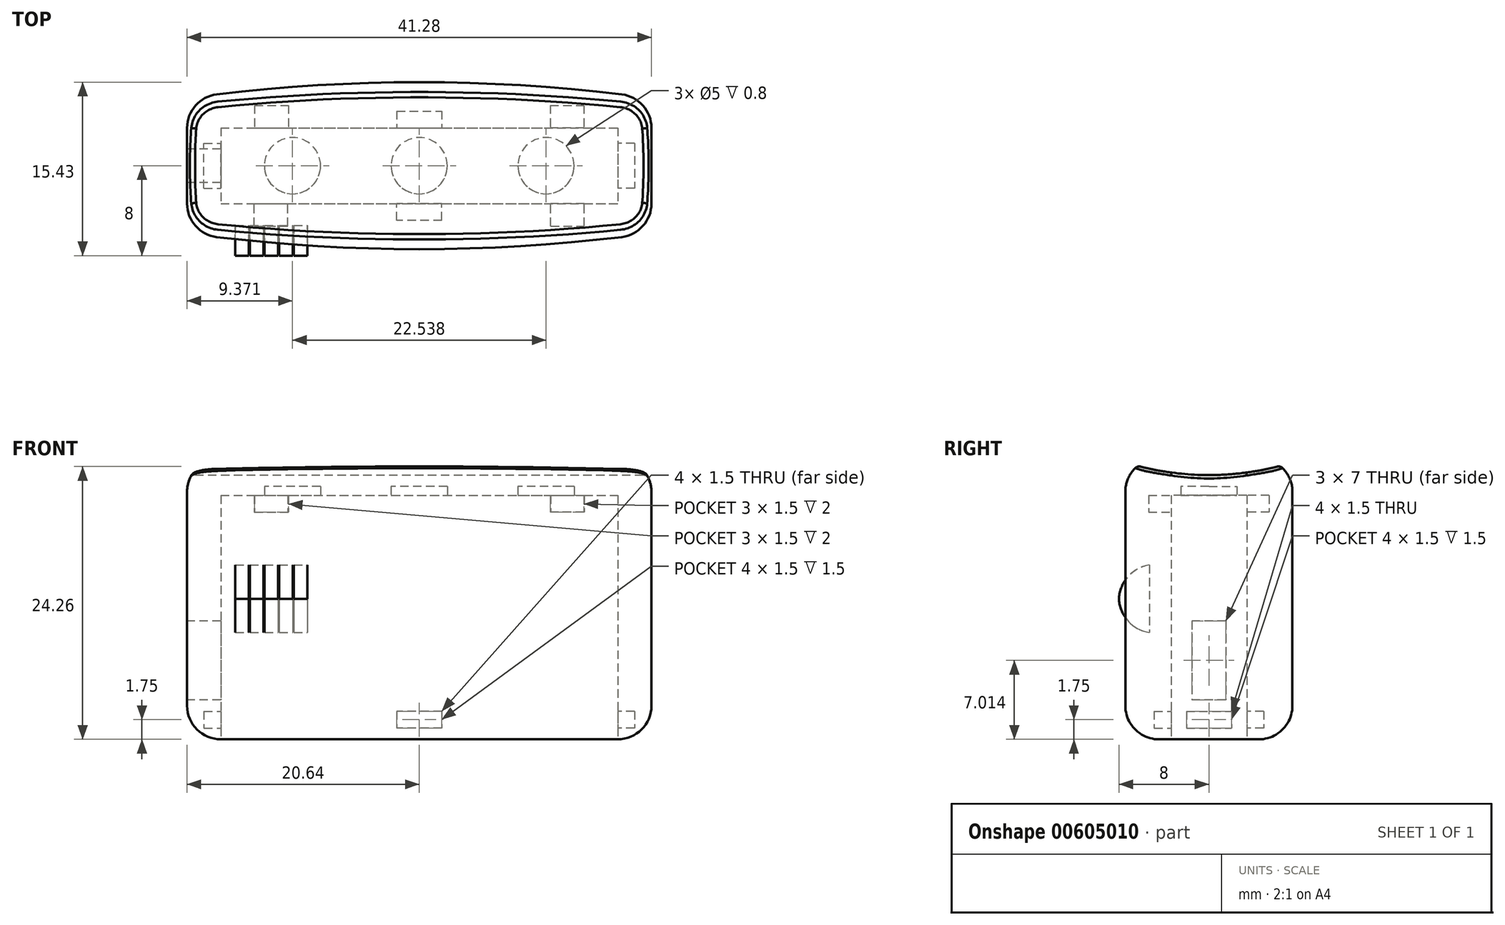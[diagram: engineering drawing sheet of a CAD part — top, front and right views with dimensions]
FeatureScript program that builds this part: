
annotation { "Feature Type Name" : "Feature", "Feature Type Description" : "" }
export const myFeature = defineFeature(function(context is Context, id is Id, definition is map)
    precondition{}
    {
        {
            var Q0;
            Q0=qCreatedBy(makeId("Top.planeOp"),FACE);
            var sketch = newSketch(context, id + "F0", { "sketchPlane" : qUnion([Q0])});
            skLineSegment(sketch, "E0", {"start": v(-20.64, 6) * mm, "end": v(-20.64, -6) * mm});
            skLineSegment(sketch, "E1", {"start": v(20.64, 6) * mm, "end": v(20.64, -6) * mm});
            skArc(sketch, "E2", {"start": v(20.64, 6) * mm, "mid": v(0, 7.43) * mm, "end": v(-20.64, 6) * mm});
            skArc(sketch, "E3.MirrorCS", {"start": v(20.64, -6) * mm, "mid": v(0, -7.43) * mm, "end": v(-20.64, -6) * mm});
            skSolve(sketch);
        }
        {
            var Q0;
            Q0 = qSketchRegion(id + "F0", true);
            extrude(context, id + "F1", {"entities" : qUnion([Q0]), "depth" : 25 * mm, "offsetDistance" : 25 * mm});
        }
        {
            var Q0;
            Q0=makeQuery(id+"F1.opExtrude","SWEPT_EDGE",EDGE,{"disambiguationData":[OSD([sQuery(id+"F0.wireOp",EDGE,"E0"),sQuery(id+"F0.wireOp",EDGE,"E2")])]});
            var Q1;
            Q1=makeQuery(id+"F1.opExtrude","SWEPT_EDGE",EDGE,{"disambiguationData":[OSD([sQuery(id+"F0.wireOp",EDGE,"E0"),sQuery(id+"F0.wireOp",EDGE,"E3.MirrorCS")])]});
            var Q2;
            Q2=makeQuery(id+"F1.opExtrude","SWEPT_EDGE",EDGE,{"disambiguationData":[OSD([sQuery(id+"F0.wireOp",EDGE,"E1"),sQuery(id+"F0.wireOp",EDGE,"E2")])]});
            var Q3;
            Q3=makeQuery(id+"F1.opExtrude","SWEPT_EDGE",EDGE,{"disambiguationData":[OSD([sQuery(id+"F0.wireOp",EDGE,"E1"),sQuery(id+"F0.wireOp",EDGE,"E3.MirrorCS")])]});
            var Q4;
            Q4=makeQuery(id+"F1.opExtrude","CAP_EDGE",EDGE,{"disambiguationData":[OSD([sQuery(id+"F0.wireOp",EDGE,"E2")])],"isStart":true});
            var Q5;
            Q5=makeQuery(id+"F1.opExtrude","CAP_EDGE",EDGE,{"disambiguationData":[OSD([sQuery(id+"F0.wireOp",EDGE,"E3.MirrorCS")])],"isStart":true});
            var Q6;
            Q6=makeQuery(id+"F1.opExtrude","CAP_EDGE",EDGE,{"disambiguationData":[OSD([sQuery(id+"F0.wireOp",EDGE,"E0")])],"isStart":true});
            var Q7;
            Q7=makeQuery(id+"F1.opExtrude","CAP_EDGE",EDGE,{"disambiguationData":[OSD([sQuery(id+"F0.wireOp",EDGE,"E1")])],"isStart":true});
            var Q8;
            Q8=makeQuery(id+"F1.opExtrude","CAP_FACE",FACE,{"disambiguationData":[OSD([sQuery(id+"F0.wireOp",EDGE,"E0"),sQuery(id+"F0.wireOp",EDGE,"E1"),sQuery(id+"F0.wireOp",EDGE,"E2"),sQuery(id+"F0.wireOp",EDGE,"E3.MirrorCS")])],"isStart":false});
            fillet(context, id + "F2", {"entities" : qUnion([Q0, Q1, Q2, Q3, Q4, Q5, Q6, Q7, Q8]), "radius" : 3 * mm, "tangentPropagation" : true, "allowEdgeOverflow" : false});
        }
        {
            var Q0;
            Q0=makeQuery(id+"F1.opExtrude","SWEPT_FACE",FACE,{"disambiguationData":[OSD([sQuery(id+"F0.wireOp",EDGE,"E1")])]});
            var sketch = newSketch(context, id + "F3", { "sketchPlane" : qUnion([Q0])});
            skCircle(sketch, "E4", {"center": v(0, 48.5) * mm, "radius": 25 * mm});
            skSolve(sketch);
        }
        {
            var Q0;
            Q0 = qSketchRegion(id + "F3", true);
            extrude(context, id + "F4", {"entities" : qUnion([Q0]), "operationType" : NewBodyOperationType.REMOVE, "oppositeDirection" : true, "depth" : 48.9 * mm, "offsetDistance" : 25 * mm});
        }
        {
            var Q0;
            Q0=makeQuery(id+"F1.opExtrude","CAP_FACE",FACE,{"disambiguationData":[OSD([sQuery(id+"F0.wireOp",EDGE,"E0"),sQuery(id+"F0.wireOp",EDGE,"E1"),sQuery(id+"F0.wireOp",EDGE,"E2"),sQuery(id+"F0.wireOp",EDGE,"E3.MirrorCS")])],"isStart":true});
            var sketch = newSketch(context, id + "F5", { "sketchPlane" : qUnion([Q0])});
            skLineSegment(sketch, "E5.bottom", {"start": v(-17.64, 3.36) * mm, "end": v(17.64, 3.36) * mm});
            skLineSegment(sketch, "E5.top", {"start": v(-17.64, -3.36) * mm, "end": v(17.64, -3.36) * mm});
            skLineSegment(sketch, "E5.left", {"start": v(-17.64, 3.36) * mm, "end": v(-17.64, -3.36) * mm});
            skLineSegment(sketch, "E5.right", {"start": v(17.64, 3.36) * mm, "end": v(17.64, -3.36) * mm});
            skSolve(sketch);
        }
        {
            var Q0;
            Q0 = qSketchRegion(id + "F5", true);
            extrude(context, id + "F6", {"entities" : qUnion([Q0]), "operationType" : NewBodyOperationType.REMOVE, "oppositeDirection" : true, "depth" : 21.7 * mm, "offsetDistance" : 25 * mm});
        }
        {
            var Q0;
            Q0=makeQuery(id+"F1.opExtrude","SWEPT_FACE",FACE,{"disambiguationData":[OSD([sQuery(id+"F0.wireOp",EDGE,"E0")])]});
            var sketch = newSketch(context, id + "F7", { "sketchPlane" : qUnion([Q0])});
            skLineSegment(sketch, "E6.bottom", {"start": v(-1.5, 10.51) * mm, "end": v(1.5, 10.51) * mm});
            skLineSegment(sketch, "E6.top", {"start": v(-1.5, 3.51) * mm, "end": v(1.5, 3.51) * mm});
            skLineSegment(sketch, "E6.left", {"start": v(-1.5, 10.51) * mm, "end": v(-1.5, 3.51) * mm});
            skLineSegment(sketch, "E6.right", {"start": v(1.5, 10.51) * mm, "end": v(1.5, 3.51) * mm});
            skSolve(sketch);
        }
        {
            var Q0;
            Q0 = qSketchRegion(id + "F7", true);
            extrude(context, id + "F8", {"entities" : qUnion([Q0]), "operationType" : NewBodyOperationType.REMOVE, "oppositeDirection" : true, "depth" : 25 * mm, "offsetDistance" : 25 * mm});
        }
        {
            var Q0;
            Q0=makeQuery(id+"F4.boolean.opBoolean","COPY",FACE,{"derivedFrom":makeQuery(id+"F4.opExtrude","SWEPT_FACE",FACE,{"disambiguationData":[OSD([sQuery(id+"F3.wireOp",EDGE,"E4")])]})});
            fillet(context, id + "F9", {"entities" : qUnion([Q0]), "radius" : 0.5 * mm, "tangentPropagation" : true, "allowEdgeOverflow" : false});
        }
        {
            var Q0;
            Q0=qCreatedBy(makeId("Front.planeOp"),FACE);
            var sketch = newSketch(context, id + "F10", { "sketchPlane" : qUnion([Q0])});
            skLineSegment(sketch, "E7.bottom", {"start": v(-15.04, 15.5) * mm, "end": v(-13.84, 15.5) * mm});
            skLineSegment(sketch, "E7.top", {"start": v(-15.04, 9.5) * mm, "end": v(-13.84, 9.5) * mm});
            skLineSegment(sketch, "E7.left", {"start": v(-15.04, 15.5) * mm, "end": v(-15.04, 9.5) * mm});
            skLineSegment(sketch, "E7.right", {"start": v(-13.84, 15.5) * mm, "end": v(-13.84, 9.5) * mm});
            skLineSegment(sketch, "E8.bottom", {"start": v(-13.74, 15.5) * mm, "end": v(-12.54, 15.5) * mm});
            skLineSegment(sketch, "E8.top", {"start": v(-13.74, 9.5) * mm, "end": v(-12.54, 9.5) * mm});
            skLineSegment(sketch, "E8.left", {"start": v(-13.74, 15.5) * mm, "end": v(-13.74, 9.5) * mm});
            skLineSegment(sketch, "E8.right", {"start": v(-12.54, 15.5) * mm, "end": v(-12.54, 9.5) * mm});
            skLineSegment(sketch, "E9.bottom", {"start": v(-12.44, 15.5) * mm, "end": v(-11.24, 15.5) * mm});
            skLineSegment(sketch, "E9.top", {"start": v(-12.44, 9.5) * mm, "end": v(-11.24, 9.5) * mm});
            skLineSegment(sketch, "E9.left", {"start": v(-12.44, 15.5) * mm, "end": v(-12.44, 9.5) * mm});
            skLineSegment(sketch, "E9.right", {"start": v(-11.24, 15.5) * mm, "end": v(-11.24, 9.5) * mm});
            skLineSegment(sketch, "E10.bottom", {"start": v(-11.14, 15.5) * mm, "end": v(-9.94, 15.5) * mm});
            skLineSegment(sketch, "E10.top", {"start": v(-11.14, 9.5) * mm, "end": v(-9.94, 9.5) * mm});
            skLineSegment(sketch, "E10.left", {"start": v(-11.14, 15.5) * mm, "end": v(-11.14, 9.5) * mm});
            skLineSegment(sketch, "E10.right", {"start": v(-9.94, 15.5) * mm, "end": v(-9.94, 9.5) * mm});
            skLineSegment(sketch, "E11.bottom", {"start": v(-16.34, 15.5) * mm, "end": v(-15.14, 15.5) * mm});
            skLineSegment(sketch, "E11.top", {"start": v(-16.34, 9.5) * mm, "end": v(-15.14, 9.5) * mm});
            skLineSegment(sketch, "E11.left", {"start": v(-16.34, 15.5) * mm, "end": v(-16.34, 9.5) * mm});
            skLineSegment(sketch, "E11.right", {"start": v(-15.14, 15.5) * mm, "end": v(-15.14, 9.5) * mm});
            skLineSegment(sketch, "E12.left", {"start": v(-9.94, 13) * mm, "end": v(-9.94, 11.9) * mm});
            skSolve(sketch);
        }
        {
            var Q0;
            Q0 = qSketchRegion(id + "F10", true);
            extrude(context, id + "F11", {"entities" : qUnion([Q0]), "depth" : 8 * mm, "offsetDistance" : 25 * mm, "hasSecondDirection" : true, "secondDirectionOppositeDirection" : false, "secondDirectionDepth" : 5.3 * mm});
        }
        {
            var Q0;
            Q0=makeQuery(id+"F11.opExtrude","CAP_EDGE",EDGE,{"disambiguationData":[OSD([sQuery(id+"F10.wireOp",EDGE,"E11.bottom")])],"isStart":false});
            var Q1;
            Q1=makeQuery(id+"F11.opExtrude","CAP_EDGE",EDGE,{"disambiguationData":[OSD([sQuery(id+"F10.wireOp",EDGE,"E7.bottom")])],"isStart":false});
            var Q2;
            Q2=makeQuery(id+"F11.opExtrude","CAP_EDGE",EDGE,{"disambiguationData":[OSD([sQuery(id+"F10.wireOp",EDGE,"E8.bottom")])],"isStart":false});
            var Q3;
            Q3=makeQuery(id+"F11.opExtrude","CAP_EDGE",EDGE,{"disambiguationData":[OSD([sQuery(id+"F10.wireOp",EDGE,"E9.bottom")])],"isStart":false});
            var Q4;
            Q4=makeQuery(id+"F11.opExtrude","CAP_EDGE",EDGE,{"disambiguationData":[OSD([sQuery(id+"F10.wireOp",EDGE,"E10.bottom")])],"isStart":false});
            var Q5;
            Q5=makeQuery(id+"F11.opExtrude","CAP_EDGE",EDGE,{"disambiguationData":[OSD([sQuery(id+"F10.wireOp",EDGE,"E10.top")])],"isStart":false});
            var Q6;
            Q6=makeQuery(id+"F11.opExtrude","CAP_EDGE",EDGE,{"disambiguationData":[OSD([sQuery(id+"F10.wireOp",EDGE,"E9.top")])],"isStart":false});
            var Q7;
            Q7=makeQuery(id+"F11.opExtrude","CAP_EDGE",EDGE,{"disambiguationData":[OSD([sQuery(id+"F10.wireOp",EDGE,"E8.top")])],"isStart":false});
            var Q8;
            Q8=makeQuery(id+"F11.opExtrude","CAP_EDGE",EDGE,{"disambiguationData":[OSD([sQuery(id+"F10.wireOp",EDGE,"E7.top")])],"isStart":false});
            var Q9;
            Q9=makeQuery(id+"F11.opExtrude","CAP_EDGE",EDGE,{"disambiguationData":[OSD([sQuery(id+"F10.wireOp",EDGE,"E11.top")])],"isStart":false});
            fillet(context, id + "F12", {"entities" : qUnion([Q0, Q1, Q2, Q3, Q4, Q5, Q6, Q7, Q8, Q9]), "radius" : 3.2 * mm, "tangentPropagation" : true, "allowEdgeOverflow" : false});
        }
        {
            var Q0;
            Q0=qCreatedBy(makeId("Top.planeOp"),FACE);
            var sketch = newSketch(context, id + "F13", { "sketchPlane" : qUnion([Q0])});
            skCircle(sketch, "E13", {"center": v(-11.27, 0) * mm, "radius": 2.5 * mm});
            skCircle(sketch, "E14", {"center": v(0, 0) * mm, "radius": 2.5 * mm});
            skCircle(sketch, "E15.MirrorC", {"center": v(11.27, 0) * mm, "radius": 2.5 * mm});
            skSolve(sketch);
        }
        {
            var Q0;
            Q0 = qSketchRegion(id + "F13", true);
            extrude(context, id + "F14", {"entities" : qUnion([Q0]), "operationType" : NewBodyOperationType.REMOVE, "depth" : 22.5 * mm, "offsetDistance" : 25 * mm});
        }
        {
            var Q0;
            Q0=makeQuery(id+"F6.boolean.opBoolean","COPY",FACE,{"derivedFrom":makeQuery(id+"F6.opExtrude","SWEPT_FACE",FACE,{"disambiguationData":[OSD([sQuery(id+"F5.wireOp",EDGE,"E5.top")])]})});
            var sketch = newSketch(context, id + "F15", { "sketchPlane" : qUnion([Q0])});
            skLineSegment(sketch, "E16.bottom", {"start": v(-14.64, 21.7) * mm, "end": v(-11.64, 21.7) * mm});
            skLineSegment(sketch, "E16.top", {"start": v(-14.64, 20.2) * mm, "end": v(-11.64, 20.2) * mm});
            skLineSegment(sketch, "E16.left", {"start": v(-14.64, 21.7) * mm, "end": v(-14.64, 20.2) * mm});
            skLineSegment(sketch, "E16.right", {"start": v(-11.64, 21.7) * mm, "end": v(-11.64, 20.2) * mm});
            skLineSegment(sketch, "E17.MirrorCS", {"start": v(14.64, 20.2) * mm, "end": v(11.64, 20.2) * mm});
            skLineSegment(sketch, "E18.MirrorCS", {"start": v(11.64, 21.7) * mm, "end": v(11.64, 20.2) * mm});
            skLineSegment(sketch, "E19.MirrorCS", {"start": v(14.64, 21.7) * mm, "end": v(14.64, 20.2) * mm});
            skLineSegment(sketch, "E20", {"start": v(11.64, 21.7) * mm, "end": v(14.64, 21.7) * mm});
            skSolve(sketch);
        }
        {
            var Q0;
            Q0 = qSketchRegion(id + "F15", true);
            extrude(context, id + "F16", {"entities" : qUnion([Q0]), "operationType" : NewBodyOperationType.REMOVE, "oppositeDirection" : true, "depth" : 2 * mm, "offsetDistance" : 25 * mm});
        }
        {
            var Q0;
            Q0=makeQuery(id+"F6.boolean.opBoolean","COPY",FACE,{"derivedFrom":makeQuery(id+"F6.opExtrude","SWEPT_FACE",FACE,{"disambiguationData":[OSD([sQuery(id+"F5.wireOp",EDGE,"E5.bottom")])]})});
            var sketch = newSketch(context, id + "F17", { "sketchPlane" : qUnion([Q0])});
            skLineSegment(sketch, "E21.bottom", {"start": v(-14.68, 21.7) * mm, "end": v(-11.68, 21.7) * mm});
            skLineSegment(sketch, "E21.top", {"start": v(-14.68, 20.2) * mm, "end": v(-11.68, 20.2) * mm});
            skLineSegment(sketch, "E21.left", {"start": v(-14.68, 21.7) * mm, "end": v(-14.68, 20.2) * mm});
            skLineSegment(sketch, "E21.right", {"start": v(-11.68, 21.7) * mm, "end": v(-11.68, 20.2) * mm});
            skLineSegment(sketch, "E22.MirrorCS", {"start": v(14.68, 21.7) * mm, "end": v(11.68, 21.7) * mm});
            skLineSegment(sketch, "E23.MirrorCS", {"start": v(14.68, 20.2) * mm, "end": v(11.68, 20.2) * mm});
            skLineSegment(sketch, "E24.MirrorCS", {"start": v(14.68, 21.7) * mm, "end": v(14.68, 20.2) * mm});
            skLineSegment(sketch, "E25.MirrorCS", {"start": v(11.68, 21.7) * mm, "end": v(11.68, 20.2) * mm});
            skSolve(sketch);
        }
        {
            var Q0;
            Q0 = qSketchRegion(id + "F17", true);
            extrude(context, id + "F18", {"entities" : qUnion([Q0]), "operationType" : NewBodyOperationType.REMOVE, "oppositeDirection" : true, "depth" : 2 * mm, "offsetDistance" : 25 * mm});
        }
        {
            var Q0;
            Q0=makeQuery(id+"F6.boolean.opBoolean","COPY",FACE,{"derivedFrom":makeQuery(id+"F6.opExtrude","SWEPT_FACE",FACE,{"disambiguationData":[OSD([sQuery(id+"F5.wireOp",EDGE,"E5.right")])]})});
            var sketch = newSketch(context, id + "F19", { "sketchPlane" : qUnion([Q0])});
            skLineSegment(sketch, "E26.bottom", {"start": v(-2, 2.5) * mm, "end": v(2, 2.5) * mm});
            skLineSegment(sketch, "E26.top", {"start": v(-2, 1) * mm, "end": v(2, 1) * mm});
            skLineSegment(sketch, "E26.left", {"start": v(-2, 2.5) * mm, "end": v(-2, 1) * mm});
            skLineSegment(sketch, "E26.right", {"start": v(2, 2.5) * mm, "end": v(2, 1) * mm});
            skSolve(sketch);
        }
        {
            var Q0;
            Q0 = qSketchRegion(id + "F19", true);
            extrude(context, id + "F20", {"entities" : qUnion([Q0]), "operationType" : NewBodyOperationType.REMOVE, "oppositeDirection" : true, "depth" : 1.5 * mm, "offsetDistance" : 25 * mm});
        }
        {
            var Q0;
            Q0=makeQuery(id+"F6.boolean.opBoolean","COPY",FACE,{"derivedFrom":makeQuery(id+"F6.opExtrude","SWEPT_FACE",FACE,{"disambiguationData":[OSD([sQuery(id+"F5.wireOp",EDGE,"E5.left")])]})});
            var sketch = newSketch(context, id + "F21", { "sketchPlane" : qUnion([Q0])});
            skLineSegment(sketch, "E27.bottom", {"start": v(-2, 2.5) * mm, "end": v(2, 2.5) * mm});
            skLineSegment(sketch, "E27.top", {"start": v(-2, 1) * mm, "end": v(2, 1) * mm});
            skLineSegment(sketch, "E27.left", {"start": v(-2, 2.5) * mm, "end": v(-2, 1) * mm});
            skLineSegment(sketch, "E27.right", {"start": v(2, 2.5) * mm, "end": v(2, 1) * mm});
            skSolve(sketch);
        }
        {
            var Q0;
            Q0 = qSketchRegion(id + "F21", true);
            extrude(context, id + "F22", {"entities" : qUnion([Q0]), "operationType" : NewBodyOperationType.REMOVE, "oppositeDirection" : true, "depth" : 1.5 * mm, "offsetDistance" : 25 * mm});
        }
        {
            var Q0;
            Q0=makeQuery(id+"F6.boolean.opBoolean","COPY",FACE,{"derivedFrom":makeQuery(id+"F6.opExtrude","SWEPT_FACE",FACE,{"disambiguationData":[OSD([sQuery(id+"F5.wireOp",EDGE,"E5.top")])]})});
            var sketch = newSketch(context, id + "F23", { "sketchPlane" : qUnion([Q0])});
            skLineSegment(sketch, "E28.bottom", {"start": v(-2, 2.5) * mm, "end": v(2, 2.5) * mm});
            skLineSegment(sketch, "E28.top", {"start": v(-2, 1) * mm, "end": v(2, 1) * mm});
            skLineSegment(sketch, "E28.left", {"start": v(-2, 2.5) * mm, "end": v(-2, 1) * mm});
            skLineSegment(sketch, "E28.right", {"start": v(2, 2.5) * mm, "end": v(2, 1) * mm});
            skSolve(sketch);
        }
        {
            var Q0;
            Q0 = qSketchRegion(id + "F23", true);
            extrude(context, id + "F24", {"entities" : qUnion([Q0]), "operationType" : NewBodyOperationType.REMOVE, "oppositeDirection" : true, "depth" : 1.5 * mm, "offsetDistance" : 25 * mm});
        }
        {
            var Q0;
            Q0=makeQuery(id+"F6.boolean.opBoolean","COPY",FACE,{"derivedFrom":makeQuery(id+"F6.opExtrude","SWEPT_FACE",FACE,{"disambiguationData":[OSD([sQuery(id+"F5.wireOp",EDGE,"E5.bottom")])]})});
            var sketch = newSketch(context, id + "F25", { "sketchPlane" : qUnion([Q0])});
            skLineSegment(sketch, "E29.bottom", {"start": v(-2, 2.5) * mm, "end": v(2, 2.5) * mm});
            skLineSegment(sketch, "E29.top", {"start": v(-2, 1) * mm, "end": v(2, 1) * mm});
            skLineSegment(sketch, "E29.left", {"start": v(-2, 2.5) * mm, "end": v(-2, 1) * mm});
            skLineSegment(sketch, "E29.right", {"start": v(2, 2.5) * mm, "end": v(2, 1) * mm});
            skSolve(sketch);
        }
        {
            var Q0;
            Q0 = qSketchRegion(id + "F25", true);
            extrude(context, id + "F26", {"entities" : qUnion([Q0]), "operationType" : NewBodyOperationType.REMOVE, "oppositeDirection" : true, "depth" : 1.5 * mm, "offsetDistance" : 25 * mm});
        }
    });
